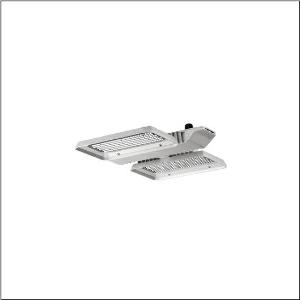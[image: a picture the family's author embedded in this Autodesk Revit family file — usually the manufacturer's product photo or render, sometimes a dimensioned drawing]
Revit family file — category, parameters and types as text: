
# Revit family: highbay_11_51hla2d14fcad
name_source: partatom
category: Lighting Fixtures
units: mm (PartAtom-declared; Revit-internal decimal feet)

## family parameters
Cut with Voids When Loaded = No
Host = Face
Light Source = No
Part Type = Normal
Room Calculation Point = No
Round Connector Dimension = Use Diameter
Shared = No

## types (1)
- --- (1 x LED, 2160 lm, 14 W, 4000K)
    Apparent Load = 14 VA
    CIE Flux Codes = 89 96 99 100 100
    Color Rendering = 80
    Color Temperature = 4000K
    Default Elevation = 1800 mm
    Description = Highbay 11, LED high bay luminaire, primary light control with lens, of PMMA, light emission: direct distribution, primary light characteristic: symmetric, installation type: suspended mounting, surface-mounted, for 1x 2x LED, rated luminous flux: 14.400lm, luminous efficacy: 177lm/W, light colour: 840, colour temperature: 4000K, control gear: ECG DALI, with terminal, 5-pole, max. 2.5mm², mains connection: 230..240V, AC/DC, 50/60Hz, rated input power: 81W, LED unit, of diecast aluminium, bead blasted, unplated, silver, length: 470mm, width: 500mm, height: 65mm, housing, of diecast aluminium, bead blasted, uncoated, silver, protection rating (complete): IP65, insulation class (complete): insulation class I (protective earthing), certification: CE, UKCA, protection symbol: D, impact resistance: IK08 with glass or PC cover, permissible operating ambient temperature: -35..+55°C, standard: EN 60598-2-22, reducing of maximum allowable ambient temperature of 5°C with ceiling mounting, corresponds to IFS (International Featured Standards) requirements for safety and quality in the food industry, packaging unit: 1 piece
    Height = 95 mm
    Lamp = 1 x LED
    Lamp Light Flux = 2160 lm
    Lamp Power = 14 W
    Lamp count = 1
    Length = 468 mm
    Luminous efficacy = 154 lm/W
    Manufacturer = Siteco
    ModVariant = No
    Model = 51HLA2D14FCAD
    Mounting Place = Ceiling
    Mounting Type = Pendant
    Number of Poles = 1
    OnlyDefault = Yes
    Power Factor = 1
    Product Name = Highbay 11
    Product group = LED high bay luminaire
    ProductGroupID = 903
    Protection Class = Protection class I
    Protection Degree = IP 65
    RLX_Detail_Level = 1
    RLX_Emergency_Light_Flux = 0 lm
    RLX_Emergency_Type = 0
    RLX_Emergency_Type_DB = No
    RlxData = <blob elided: 86801 chars, md5=6a1d7336>
    Socket = socket
    Standby Power = 0 W
    System Light Flux = 2160 lm
    System Power = 14 W
    Type Comments = : central accumulator DC – ECG emengency level 15%
    Type Image = l_1003425.jpg
    URL = http://relux.com
    VarID = @adj_135357
    Voltage = 0 V
    Weight = 0.00 kg
    Width = 501 mm

## geometry (parser evidence)
native form markers: Blend x4, Sweep x11
no freeform markers — native parametric forms only
